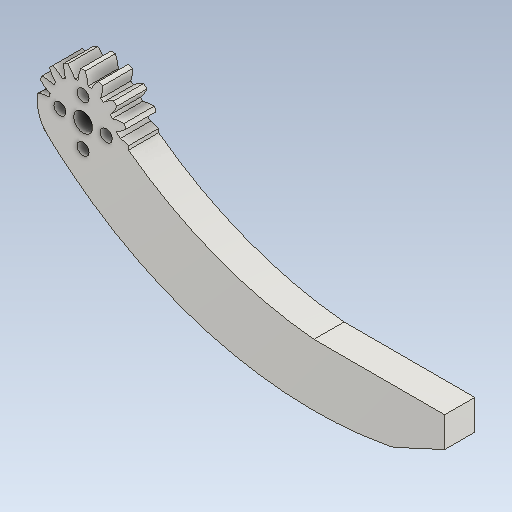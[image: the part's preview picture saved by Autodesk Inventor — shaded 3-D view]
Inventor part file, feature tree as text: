
AUTODESK INVENTOR PART (.ipt)
format: ipt  version: 2020.1 (Build 241239000, 239)  size: 230,912 bytes
history: native  units: in
note: dims shown in document units (in); Inventor stores cm internally (conversion verified against a paired STEP export)
features: sketch x17, other x12, plane x3
ambient origin geometry x8: Origin, YZ Plane, XZ Plane, XY Plane, X Axis, Y Axis, Z Axis, Center Point
bodies: Solid1 (feature_tree)
feature tree (32):
  other  "Spur Gear1"
  other  "Solid1::Spur Gear1"
  other  "TaggingFeature1"
  sketch  "Sketch1"  dims[d0=0.3937in]
  sketch  "Sketch2"  dims[d9=0.0in d14=0.0in d15=1.3416in d16=0.0in d17=0.0in d18=0.0in d19=1.3416in]
  sketch  "Sketch3"
  sketch  "Sketch4"
  sketch  "Sketch5"
  sketch  "Sketch6"
  sketch  "Sketch7"
  sketch  "Sketch8"
  sketch  "Sketch9"
  sketch  "Sketch10"
  sketch  "Sketch11"
  sketch  "Sketch12"
  sketch  "Sketch13"
  sketch  "Sketch14"
  sketch  "Sketch15"
  sketch  "Sketch16"
  sketch  "Sketch17"
  plane  "XZ Plane_1"
  plane  "Work Plane2"
  plane  "Work Plane3"
  other  "Srf1"
  other  "Srf1::Derived"
  other  "Start plane iMate"
  other  "Distance iMate"
  other  "Position iMate"
  other  "Mesh iMate"
  other  "Axis iMate"
  other  "Mesh iMate2"
  other  "Align iMate"
